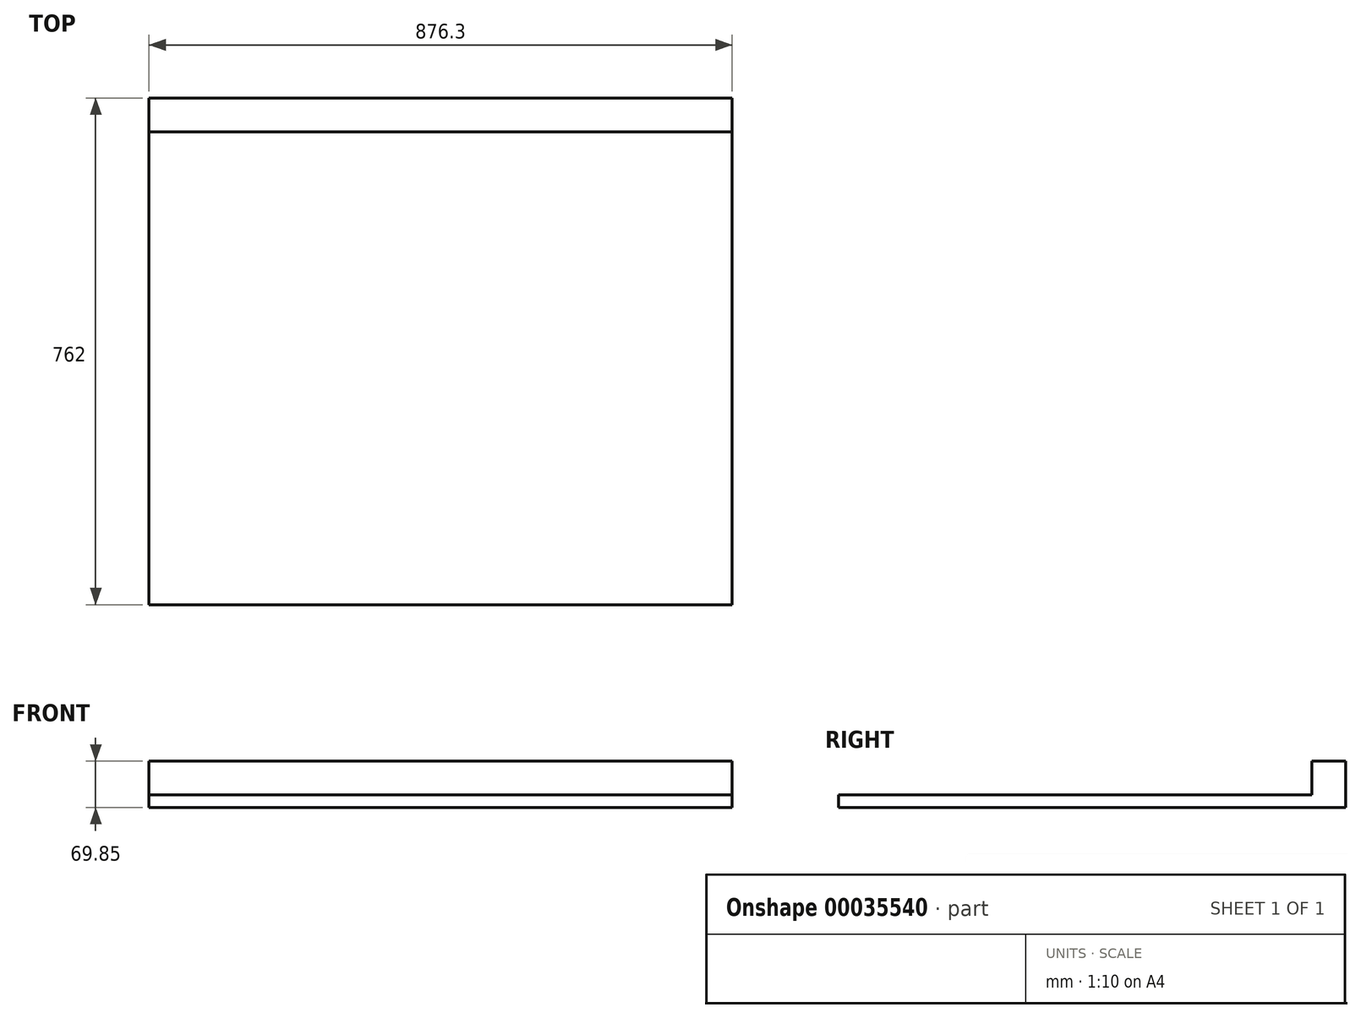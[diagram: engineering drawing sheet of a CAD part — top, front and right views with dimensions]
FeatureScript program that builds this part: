
annotation { "Feature Type Name" : "Feature", "Feature Type Description" : "" }
export const myFeature = defineFeature(function(context is Context, id is Id, definition is map)
    precondition{}
    {
        {
            var Q0;
            Q0=qCreatedBy(makeId("Top.planeOp"),FACE);
            var sketch = newSketch(context, id + "F0", { "sketchPlane" : qUnion([Q0])});
            skLineSegment(sketch, "E0.bottom", {"start": v(-436.31, 452.14) * mm, "end": v(439.99, 452.14) * mm});
            skLineSegment(sketch, "E0.top", {"start": v(-436.31, -309.86) * mm, "end": v(439.99, -309.86) * mm});
            skLineSegment(sketch, "E0.left", {"start": v(-436.31, 452.14) * mm, "end": v(-436.31, -309.86) * mm});
            skLineSegment(sketch, "E0.right", {"start": v(439.99, 452.14) * mm, "end": v(439.99, -309.86) * mm});
            skSolve(sketch);
        }
        {
            var Q0;
            Q0 = qSketchRegion(id + "F0", true);
            extrude(context, id + "F1", {"entities" : qUnion([Q0]), "depth" : 19.05 * mm});
        }
        {
            var Q0;
            Q0=makeQuery(id+"F1.opExtrude","CAP_FACE",FACE,{"disambiguationData":[OSD([sQuery(id+"F0.wireOp",EDGE,"E0.bottom"),sQuery(id+"F0.wireOp",EDGE,"E0.top"),sQuery(id+"F0.wireOp",EDGE,"E0.left"),sQuery(id+"F0.wireOp",EDGE,"E0.right")])],"isStart":false});
            var sketch = newSketch(context, id + "F2", { "sketchPlane" : qUnion([Q0])});
            skLineSegment(sketch, "E1.0", {"start": v(-436.31, 452.14) * mm, "end": v(439.99, 452.14) * mm});
            skLineSegment(sketch, "E2.0", {"start": v(-436.31, 452.14) * mm, "end": v(-436.31, 401.34) * mm});
            skLineSegment(sketch, "E3.0", {"start": v(439.99, 452.14) * mm, "end": v(439.99, 401.34) * mm});
            skLineSegment(sketch, "E4", {"start": v(-436.31, 401.34) * mm, "end": v(439.99, 401.34) * mm});
            skPoint(sketch, "E5.orphan", {"position": v(-436.31, -309.86) * mm});
            skPoint(sketch, "E6.orphan", {"position": v(439.99, -309.86) * mm});
            skSolve(sketch);
        }
        {
            var Q0;
            Q0 = qSketchRegion(id + "F2", true);
            extrude(context, id + "F3", {"entities" : qUnion([Q0]), "operationType" : NewBodyOperationType.ADD, "depth" : 50.8 * mm});
        }
    });
